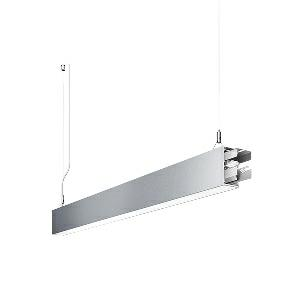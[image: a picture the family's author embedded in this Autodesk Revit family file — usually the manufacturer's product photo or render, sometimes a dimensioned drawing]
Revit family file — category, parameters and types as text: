
# Revit family: dotoo_line_-_dlp_2000_830_d_sta_00805848_20e9
name_source: partatom
category: Lighting Fixtures
units: mm (PartAtom-declared; Revit-internal decimal feet)

## family parameters
Cut with Voids When Loaded = No
Host = Face
Light Source = No
Part Type = Normal
Room Calculation Point = No
Round Connector Dimension = Use Diameter
Shared = No

## types (1)
- DOTOO.line - DLP 2000/830/D STA (1 x LED, 1650 lm, 3000K)
    Apparent Load = 16 VA
    Approval mark = CE
    CIE Flux Codes = 67 91 98 100 100
    Color Rendering = 80-89
    Color Temperature = 3000K
    Control Gear = Electronic ballast
    Default Elevation = 1800 mm
    Description = DLP 2000/830/D|Suspended luminaire|light source: LED|connected load: 220-240 V, 50/60 Hz|Power consumption: approx. 16 W|standby: approx. 0,15|luminous flux: 1650 lm|luminous efficacy: 103 lm/W|light distribution: Direct|direct ratio: approx. 100 %|colour temperature: Warm white, ca. 3000 K|color rendering index (CRI): >= 80|chromaticity tolerance:  3 SDCM|System of protection: IP 40|technology: Continuously dimmable|luminaire body|material: Sectional aluminium|colour: Silver|lamp cover: Acrylic (PMMA), Clear|mains lead: 2.00 m With free stranded wires|Fastening: Steel cable 0.3 - 0.7 m|glare control: Prism aperture|luminance(L65): <= 3000 cd/m|unified glare rating(4H 8H): <=  19|special features: DALI Load 1x, TouchDIM - dimming via standard switch, Through-wired, up to 18 m on one mains connection, Flicker-free, Suitable as emergency lighting, Start luminaire with mains connection, Mechanical and electrical connection of the individual modules without tools|
    Frequency = 50 Hz
    Height = 110 mm
    Lamp = 1 x LED
    Lamp Light Flux = 1650 lm
    Lamp count = 1
    Length = 1408 mm
    Luminous efficacy = 103 lm/W
    Manufacturer = Waldmann
    ModVariant = No
    Model = 00805848
    Mounting Place = Ceiling
    Mounting Type = Pendant
    Number of Poles = 1
    OnlyDefault = Yes
    Power Factor = 1
    Product Name = DOTOO.line - DLP 2000/830/D STA
    Product group = Suspended luminaire
    ProductGroupID = 9
    Protection Class = Protection class I
    Protection Degree = IP 40
    RLX_Detail_Level = 1
    RLX_Emergency_Light_Flux = 0 lm
    RLX_Emergency_Type = 0
    RLX_Emergency_Type_DB = No
    RlxData = <blob elided: 23661 chars, md5=a167f055>
    Socket = socket
    Standby Power = 0 W
    System Light Flux = 1650 lm
    System Power = 16 W
    Type Comments = Product without accessories
    Type Image = 113310000-00692594.jpg
    URL = http://relux.com
    VarID = ---
    Voltage = 230 V
    Voltage Range = 220-240 V
    Weight = 0.00 kg
    Width = 60 mm  [stored 0.19685 ft]

note: [stored X ft] marks values corroborated as IEEE doubles in the binary element streams (Revit-internal decimal feet)

## geometry (parser evidence)
native form markers: Blend x4, Sweep x13
no freeform markers — native parametric forms only
